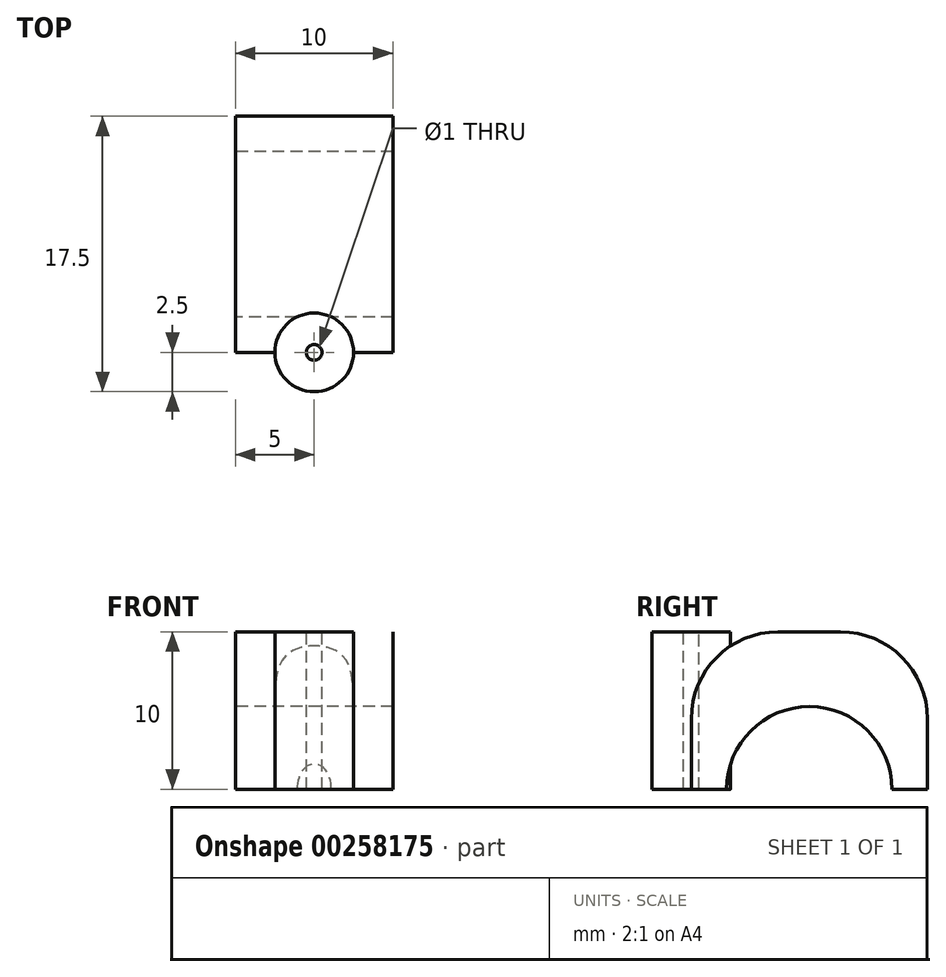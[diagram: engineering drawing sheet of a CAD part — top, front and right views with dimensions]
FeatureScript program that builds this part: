
annotation { "Feature Type Name" : "Feature", "Feature Type Description" : "" }
export const myFeature = defineFeature(function(context is Context, id is Id, definition is map)
    precondition{}
    {
        {
            var Q0;
            Q0=qCreatedBy(makeId("Top.planeOp"),FACE);
            var sketch = newSketch(context, id + "F0", { "sketchPlane" : qUnion([Q0])});
            skLineSegment(sketch, "E0", {"start": v(0, 0) * mm, "end": v(10, 0) * mm});
            skLineSegment(sketch, "E1", {"start": v(10, 0) * mm, "end": v(10, 15) * mm});
            skLineSegment(sketch, "E2", {"start": v(10, 15) * mm, "end": v(0, 15) * mm});
            skLineSegment(sketch, "E3", {"start": v(0, 15) * mm, "end": v(0, 0) * mm});
            skSolve(sketch);
        }
        {
            var Q0;
            Q0 = qSketchRegion(id + "F0", true);
            extrude(context, id + "F1", {"entities" : qUnion([Q0]), "depth" : 7.5 * mm});
        }
        {
            var Q0;
            Q0=makeQuery(id+"F1.opExtrude","SWEPT_FACE",FACE,{"disambiguationData":[OSD([sQuery(id+"F0.wireOp",EDGE,"E3")])]});
            var sketch = newSketch(context, id + "F2", { "sketchPlane" : qUnion([Q0])});
            skArc(sketch, "E4", {"start": v(-2.25, 0) * mm, "mid": v(-7.5, 5.25) * mm, "end": v(-12.75, 0) * mm});
            skLineSegment(sketch, "E5.0", {"start": v(-12.75, 0) * mm, "end": v(-2.25, 0) * mm});
            skPoint(sketch, "E6.orphan", {"position": v(-15, 0) * mm});
            skPoint(sketch, "E7.orphan", {"position": v(0, 0) * mm});
            skSolve(sketch);
        }
        {
            var Q0;
            Q0 = qSketchRegion(id + "F2", true);
            extrude(context, id + "F3", {"entities" : qUnion([Q0]), "operationType" : NewBodyOperationType.REMOVE, "endBound" : BoundingType.THROUGH_ALL, "oppositeDirection" : true, "depth" : 25.4 * mm});
        }
        {
            var Q0;
            Q0=makeQuery(id+"F1.opExtrude","CAP_FACE",FACE,{"disambiguationData":[OSD([sQuery(id+"F0.wireOp",EDGE,"E0"),sQuery(id+"F0.wireOp",EDGE,"E1"),sQuery(id+"F0.wireOp",EDGE,"E2"),sQuery(id+"F0.wireOp",EDGE,"E3")])],"isStart":false});
            var sketch = newSketch(context, id + "F4", { "sketchPlane" : qUnion([Q0])});
            skLineSegment(sketch, "E8", {"start": v(0, 15) * mm, "end": v(10, 15) * mm});
            skLineSegment(sketch, "E9", {"start": v(10, 15) * mm, "end": v(10, 0) * mm});
            skLineSegment(sketch, "E10", {"start": v(10, 0) * mm, "end": v(0, 0) * mm});
            skLineSegment(sketch, "E11", {"start": v(0, 0) * mm, "end": v(0, 15) * mm});
            skSolve(sketch);
        }
        {
            var Q0;
            Q0 = qSketchRegion(id + "F4", true);
            extrude(context, id + "F5", {"entities" : qUnion([Q0]), "operationType" : NewBodyOperationType.ADD, "depth" : 2.5 * mm});
        }
        {
            var Q0;
            Q0=makeQuery(id+"F5.opExtrude","CAP_EDGE",EDGE,{"disambiguationData":[OSD([sQuery(id+"F4.wireOp",EDGE,"E8")])],"isStart":false});
            var Q1;
            Q1=makeQuery(id+"F5.opExtrude","CAP_EDGE",EDGE,{"disambiguationData":[OSD([sQuery(id+"F4.wireOp",EDGE,"E10")])],"isStart":false});
            fillet(context, id + "F6", {"entities" : qUnion([Q0, Q1]), "radius" : 5.52 * mm, "tangentPropagation" : true, "allowEdgeOverflow" : false});
        }
        {
            var Q0;
            Q0=makeQuery(id+"F5.opExtrude","CAP_FACE",FACE,{"disambiguationData":[OSD([sQuery(id+"F4.wireOp",EDGE,"E8"),sQuery(id+"F4.wireOp",EDGE,"E9"),sQuery(id+"F4.wireOp",EDGE,"E10"),sQuery(id+"F4.wireOp",EDGE,"E11")])],"isStart":false});
            var sketch = newSketch(context, id + "F7", { "sketchPlane" : qUnion([Q0])});
            skCircle(sketch, "E12", {"center": v(5, 0) * mm, "radius": 2.5 * mm});
            skPoint(sketch, "E12.centerSnap0", {"position": v(5, 5.52) * mm});
            skCircle(sketch, "E13", {"center": v(5, 0) * mm, "radius": 0.5 * mm});
            skSolve(sketch);
        }
        {
            var Q0;
            Q0=makeQuery(id+"F7.imprint","IMPRINT",FACE,{"disambiguationData":[TD([[makeQuery(id+"F7.imprint","IMPRINT",EDGE,{"derivedFrom":sQuery(id+"F7.wireOp",EDGE,"E13")}),1.0]])]});
            extrude(context, id + "F8", {"entities" : qUnion([Q0]), "operationType" : NewBodyOperationType.REMOVE, "endBound" : BoundingType.THROUGH_ALL, "oppositeDirection" : true, "depth" : 25.4 * mm});
        }
        {
            var Q0;
            Q0=makeQuery(id+"F7.imprint","IMPRINT",FACE,{"disambiguationData":[TD([[makeQuery(id+"F7.imprint","IMPRINT",EDGE,{"derivedFrom":sQuery(id+"F7.wireOp",EDGE,"E12")}),1.0]])]});
            extrude(context, id + "F9", {"entities" : qUnion([Q0]), "operationType" : NewBodyOperationType.ADD, "oppositeDirection" : true, "depth" : 10 * mm});
        }
    });
